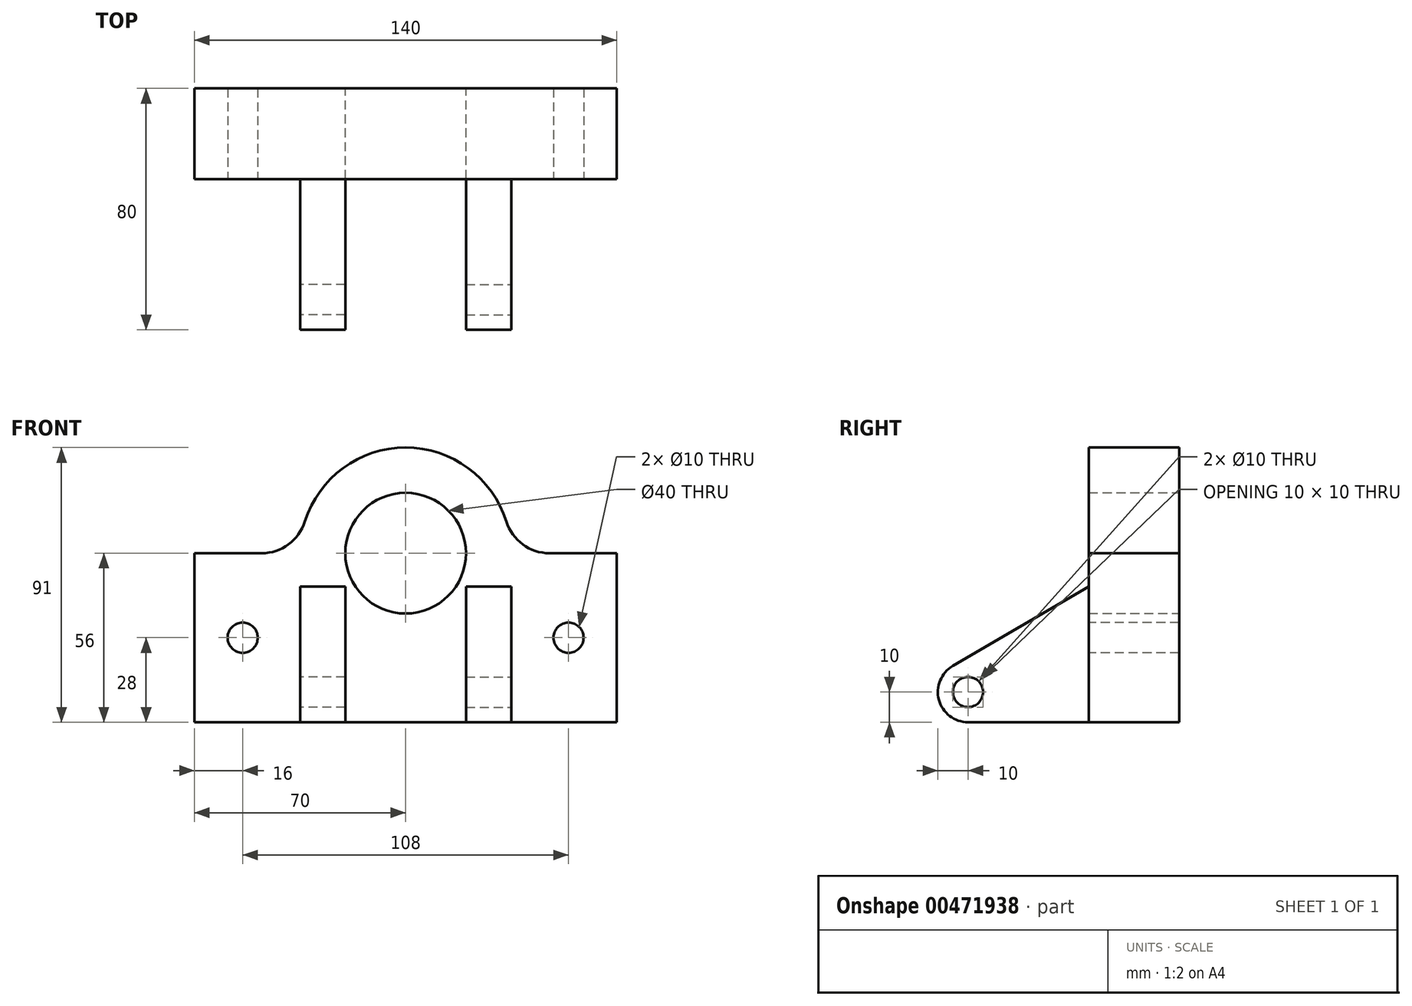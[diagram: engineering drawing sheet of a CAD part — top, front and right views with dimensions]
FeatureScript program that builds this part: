
annotation { "Feature Type Name" : "Feature", "Feature Type Description" : "" }
export const myFeature = defineFeature(function(context is Context, id is Id, definition is map)
    precondition{}
    {
        {
            var Q0;
            Q0=qCreatedBy(makeId("Front.planeOp"),FACE);
            var sketch = newSketch(context, id + "F0", { "sketchPlane" : qUnion([Q0])});
            skLineSegment(sketch, "E0.bottom", {"start": v(70, 28) * mm, "end": v(-70, 28) * mm});
            skLineSegment(sketch, "E0.top", {"start": v(70, -28) * mm, "end": v(-70, -28) * mm});
            skLineSegment(sketch, "E0.left", {"start": v(70, 28) * mm, "end": v(70, -28) * mm});
            skLineSegment(sketch, "E0.right", {"start": v(-70, 28) * mm, "end": v(-70, -28) * mm});
            skPoint(sketch, "E0.middle", {"position": v(0, 0) * mm});
            skCircle(sketch, "E1", {"center": v(0, 28) * mm, "radius": 20 * mm});
            skCircle(sketch, "E2", {"center": v(0, 28) * mm, "radius": 35 * mm});
            skSolve(sketch);
        }
        {
            var Q0;
            Q0 = qSketchRegion(id + "F0", true);
            extrude(context, id + "F1", {"entities" : qUnion([Q0]), "depth" : 30 * mm});
        }
        {
            var Q0;
            {var subQ0=sQuery(id+"F0.wireOp",EDGE,"E2");var subQ1=sQuery(id+"F0.wireOp",EDGE,"E0.bottom");Q0=makeQuery(id+"F1.opExtrude","SWEPT_EDGE",EDGE,{"disambiguationData":[OSD([subQ1,subQ0]),TDD([makeQuery(id+"F0.imprint","INTERSECT",VERTEX,{"disambiguationData":[OD(1.0)],"derivedFrom":[subQ1,subQ0]})])]});}
            var Q1;
            {var subQ0=sQuery(id+"F0.wireOp",EDGE,"E2");var subQ1=sQuery(id+"F0.wireOp",EDGE,"E0.bottom");Q1=makeQuery(id+"F1.opExtrude","SWEPT_EDGE",EDGE,{"disambiguationData":[OSD([subQ1,subQ0]),TDD([makeQuery(id+"F0.imprint","INTERSECT",VERTEX,{"disambiguationData":[OD(0.0)],"derivedFrom":[subQ1,subQ0]})])]});}
            fillet(context, id + "F2", {"entities" : qUnion([Q0, Q1]), "radius" : 15 * mm, "tangentPropagation" : true, "allowEdgeOverflow" : false});
        }
        {
            var Q0;
            Q0=makeQuery(id+"F1.opExtrude","CAP_FACE",FACE,{"disambiguationData":[OSD([sQuery(id+"F0.wireOp",EDGE,"E0.bottom"),sQuery(id+"F0.wireOp",EDGE,"E0.top"),sQuery(id+"F0.wireOp",EDGE,"E0.left"),sQuery(id+"F0.wireOp",EDGE,"E0.right"),sQuery(id+"F0.wireOp",EDGE,"E1"),sQuery(id+"F0.wireOp",EDGE,"E2")])],"isStart":false});
            var sketch = newSketch(context, id + "F3", { "sketchPlane" : qUnion([Q0])});
            skLineSegment(sketch, "E3", {"start": v(-47.7, 28) * mm, "end": v(-47.7, -28) * mm});
            skLineSegment(sketch, "E4", {"start": v(47.7, 28) * mm, "end": v(47.7, -28) * mm});
            skLineSegment(sketch, "E5", {"start": v(-70, 0) * mm, "end": v(-54, 0) * mm});
            skPoint(sketch, "E5.endSnap0", {"position": v(-70, 0) * mm});
            skCircle(sketch, "E6", {"center": v(-54, 0) * mm, "radius": 5 * mm});
            skLineSegment(sketch, "E7", {"start": v(70, 0) * mm, "end": v(54, 0) * mm});
            skPoint(sketch, "E7.endSnap0", {"position": v(70, 0) * mm});
            skCircle(sketch, "E8", {"center": v(54, 0) * mm, "radius": 5 * mm});
            skSolve(sketch);
        }
        {
            var Q0;
            Q0=makeQuery(id+"F3.imprint","IMPRINT",FACE,{"disambiguationData":[TD([[makeQuery(id+"F3.imprint","IMPRINT",EDGE,{"derivedFrom":sQuery(id+"F3.wireOp",EDGE,"E6")}),1.0]])]});
            var Q1;
            Q1=makeQuery(id+"F3.imprint","IMPRINT",FACE,{"disambiguationData":[TD([[makeQuery(id+"F3.imprint","IMPRINT",EDGE,{"derivedFrom":sQuery(id+"F3.wireOp",EDGE,"E8")}),1.0]])]});
            extrude(context, id + "F4", {"entities" : qUnion([Q0, Q1]), "operationType" : NewBodyOperationType.REMOVE, "oppositeDirection" : true, "depth" : 72 * mm});
        }
        {
            var Q0;
            {var subQ2=sQuery(id+"F3.wireOp",EDGE,"E3");Q0=makeQuery(id+"F3.imprint","IMPRINT",FACE,{"disambiguationData":[TD([[makeQuery(id+"F3.imprint","IMPRINT",EDGE,{"derivedFrom":subQ2}),1.0]])]});}
            var sketch = newSketch(context, id + "F5", { "sketchPlane" : qUnion([Q0])});
            skCircle(sketch, "E9.0.0", {"center": v(-54, 0) * mm, "radius": 5 * mm});
            skCircle(sketch, "E10.0", {"center": v(54, 0) * mm, "radius": 5 * mm});
            skLineSegment(sketch, "E11", {"start": v(-54, 0) * mm, "end": v(-35, 0) * mm});
            skLineSegment(sketch, "E12", {"start": v(54, 0) * mm, "end": v(35, 0) * mm});
            skLineSegment(sketch, "E13.0.0", {"start": v(47.7, -28) * mm, "end": v(47.7, 28) * mm});
            skArc(sketch, "E13.0.1", {"start": v(47.7, 28) * mm, "mid": v(38.82, 30.9) * mm, "end": v(33.39, 38.5) * mm});
            skArc(sketch, "E13.0.2", {"start": v(33.39, 38.5) * mm, "mid": v(0, 63) * mm, "end": v(-33.39, 38.5) * mm});
            skArc(sketch, "E13.0.3", {"start": v(-33.39, 38.5) * mm, "mid": v(-38.82, 30.9) * mm, "end": v(-47.7, 28) * mm});
            skLineSegment(sketch, "E13.0.4", {"start": v(-47.7, 28) * mm, "end": v(-47.7, -28) * mm});
            skLineSegment(sketch, "E13.0.5", {"start": v(-47.7, -28) * mm, "end": v(47.7, -28) * mm});
            skLineSegment(sketch, "E14", {"start": v(-35, -28) * mm, "end": v(-35, 17) * mm});
            skLineSegment(sketch, "E15", {"start": v(-35, 17) * mm, "end": v(-20, 17) * mm});
            skLineSegment(sketch, "E16", {"start": v(-20, 17) * mm, "end": v(-20, -28) * mm});
            skLineSegment(sketch, "E17", {"start": v(-20, -28) * mm, "end": v(-35, -28) * mm});
            skLineSegment(sketch, "E18.MirrorCS", {"start": v(35, 17) * mm, "end": v(20, 17) * mm});
            skLineSegment(sketch, "E19.MirrorCS", {"start": v(20, 17) * mm, "end": v(20, -28) * mm});
            skLineSegment(sketch, "E20.MirrorCS", {"start": v(35, -28) * mm, "end": v(35, 17) * mm});
            skLineSegment(sketch, "E21.MirrorCS", {"start": v(47.7, -28) * mm, "end": v(-47.7, -28) * mm});
            skLineSegment(sketch, "E22", {"start": v(20, -28) * mm, "end": v(35, -28) * mm});
            skSolve(sketch);
        }
        {
            var Q0;
            {var subQ1=sQuery(id+"F5.wireOp",EDGE,"E15");Q0=makeQuery(id+"F5.imprint","IMPRINT",FACE,{"disambiguationData":[TD([[makeQuery(id+"F5.imprint","IMPRINT",EDGE,{"derivedFrom":subQ1}),-1.0]])]});}
            extrude(context, id + "F6", {"entities" : qUnion([Q0]), "depth" : 60 * mm});
        }
        {
            var Q0;
            Q0=makeQuery(id+"F6.opExtrude","SWEPT_FACE",FACE,{"disambiguationData":[OSD([sQuery(id+"F5.wireOp",EDGE,"E14")])]});
            var sketch = newSketch(context, id + "F7", { "sketchPlane" : qUnion([Q0])});
            skLineSegment(sketch, "E23", {"start": v(30, -28) * mm, "end": v(55.38, -28) * mm});
            skLineSegment(sketch, "E24", {"start": v(30, -28) * mm, "end": v(70, -28) * mm});
            skLineSegment(sketch, "E25", {"start": v(70, -28) * mm, "end": v(70, -8) * mm});
            skCircle(sketch, "E26", {"center": v(70, -18) * mm, "radius": 5 * mm});
            skCircle(sketch, "E27", {"center": v(70, -18) * mm, "radius": 10 * mm});
            skLineSegment(sketch, "E28", {"start": v(30, 17) * mm, "end": v(75.05, -9.37) * mm});
            skSolve(sketch);
        }
        {
            var Q0;
            {var subQ5=sQuery(id+"F7.wireOp",EDGE,"E28");Q0=makeQuery(id+"F7.imprint","IMPRINT",FACE,{"disambiguationData":[TD([[makeQuery(id+"F7.imprint","IMPRINT",EDGE,{"derivedFrom":subQ5}),1.0]])]});}
            var Q1;
            {var subQ0=sQuery(id+"F7.wireOp",EDGE,"E26");var subQ1=sQuery(id+"F7.wireOp",EDGE,"E25");var subQ2=makeQuery(id+"F7.imprint","INTERSECT",VERTEX,{"disambiguationData":[OD(0.0)],"derivedFrom":[subQ1,subQ0]});Q1=makeQuery(id+"F7.imprint","IMPRINT",FACE,{"disambiguationData":[TD([[makeQuery(id+"F7.imprint","IMPRINT",EDGE,{"disambiguationData":[TD([[subQ2,-1.0]])],"derivedFrom":subQ1}),1.0]])]});}
            var Q2;
            {var subQ0=sQuery(id+"F7.wireOp",EDGE,"E26");var subQ1=sQuery(id+"F7.wireOp",EDGE,"E25");var subQ2=makeQuery(id+"F7.imprint","INTERSECT",VERTEX,{"disambiguationData":[OD(0.0)],"derivedFrom":[subQ1,subQ0]});Q2=makeQuery(id+"F7.imprint","IMPRINT",FACE,{"disambiguationData":[TD([[makeQuery(id+"F7.imprint","IMPRINT",EDGE,{"disambiguationData":[TD([[subQ2,-1.0]])],"derivedFrom":subQ1}),-1.0]])]});}
            extrude(context, id + "F8", {"entities" : qUnion([Q0, Q1, Q2]), "operationType" : NewBodyOperationType.REMOVE, "oppositeDirection" : true, "depth" : 51.3 * mm});
        }
        {
            var Q0;
            Q0=makeQuery(id+"F6.opExtrude","SWEPT_BODY",BODY,{"disambiguationData":[OSD([sQuery(id+"F5.wireOp",EDGE,"E14"),sQuery(id+"F5.wireOp",EDGE,"E15"),sQuery(id+"F5.wireOp",EDGE,"E16"),sQuery(id+"F5.wireOp",EDGE,"E21.MirrorCS")])]});
            var Q1;
            Q1=qCreatedBy(makeId("Right.planeOp"),FACE);
            mirror(context, id + "F9", {"operationType" : NewBodyOperationType.ADD, "entities" : qUnion([Q0]), "mirrorPlane" : qUnion([Q1])});
        }
    });
